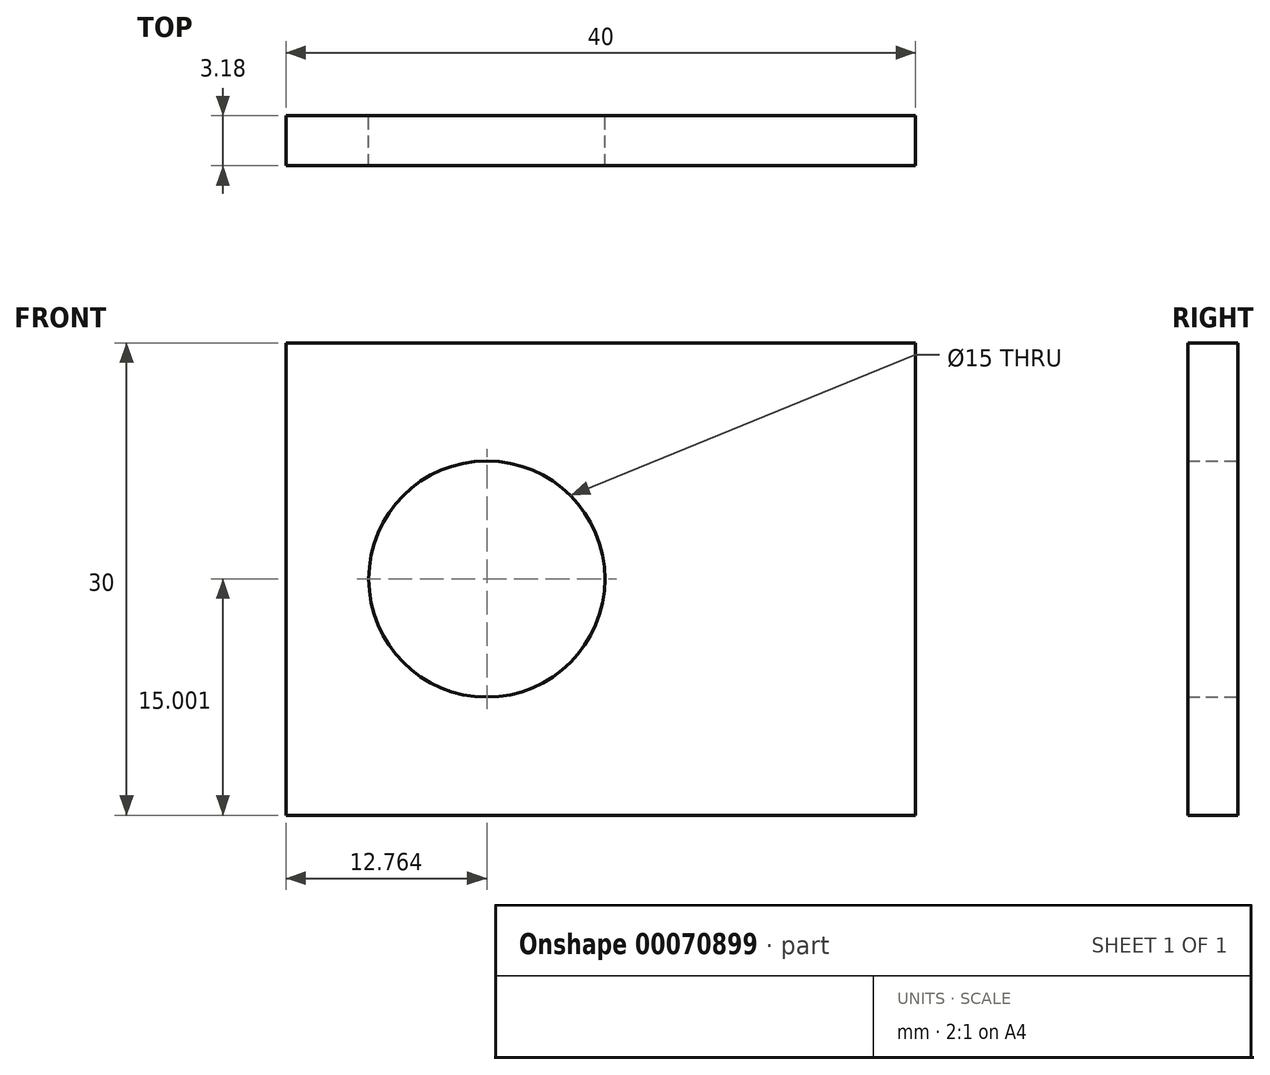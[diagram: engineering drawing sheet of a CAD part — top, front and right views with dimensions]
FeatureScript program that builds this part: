
annotation { "Feature Type Name" : "Feature", "Feature Type Description" : "" }
export const myFeature = defineFeature(function(context is Context, id is Id, definition is map)
    precondition{}
    {
        {
            var Q0;
            Q0=qCreatedBy(makeId("Front.planeOp"),FACE);
            var sketch = newSketch(context, id + "F0", { "sketchPlane" : qUnion([Q0])});
            skLineSegment(sketch, "E0.bottom", {"start": v(-49.56, 1.4) * mm, "end": v(-9.56, 1.4) * mm});
            skLineSegment(sketch, "E0.top", {"start": v(-49.56, 31.4) * mm, "end": v(-9.56, 31.4) * mm});
            skLineSegment(sketch, "E0.left", {"start": v(-49.56, 1.4) * mm, "end": v(-49.56, 31.4) * mm});
            skLineSegment(sketch, "E0.right", {"start": v(-9.56, 1.4) * mm, "end": v(-9.56, 31.4) * mm});
            skCircle(sketch, "E1", {"center": v(-36.8, 16.4) * mm, "radius": 7.5 * mm});
            skPoint(sketch, "E1.centerSnap0", {"position": v(-49.56, 16.4) * mm});
            skSolve(sketch);
        }
        {
            var Q0;
            Q0=makeQuery(id+"F0.imprint","IMPRINT",FACE,{"disambiguationData":[TD([[makeQuery(id+"F0.imprint","IMPRINT",EDGE,{"derivedFrom":sQuery(id+"F0.wireOp",EDGE,"E0.bottom")}),1.0]])]});
            extrude(context, id + "F1", {"entities" : qUnion([Q0]), "depth" : 3.17 * mm});
        }
    });
